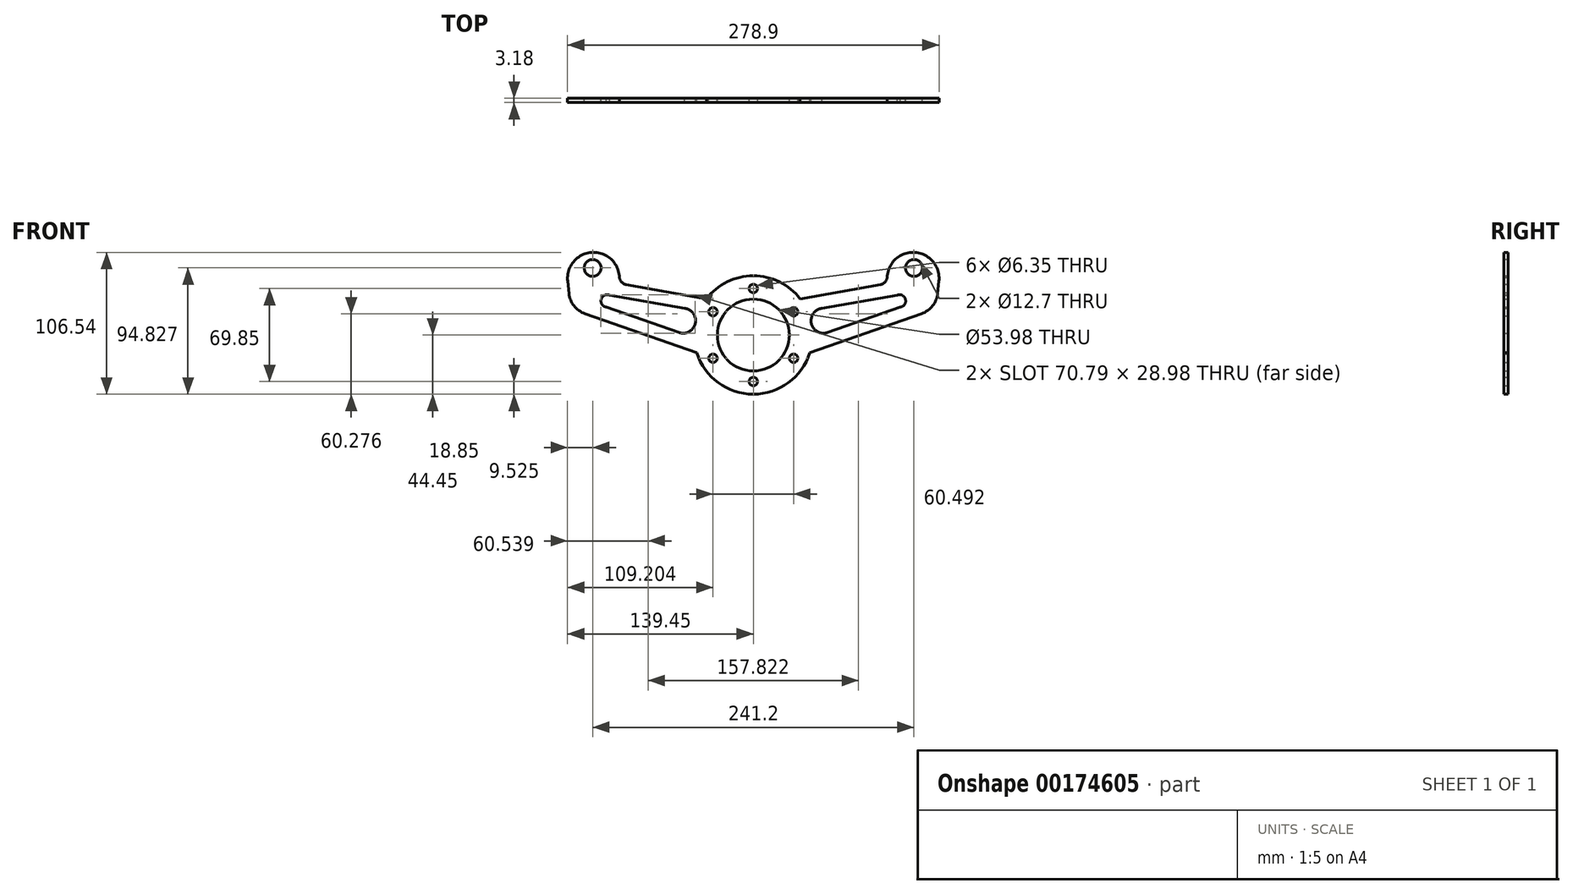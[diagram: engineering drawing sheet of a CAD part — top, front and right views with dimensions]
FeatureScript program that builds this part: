
annotation { "Feature Type Name" : "Feature", "Feature Type Description" : "" }
export const myFeature = defineFeature(function(context is Context, id is Id, definition is map)
    precondition{}
    {
        {
            var Q0;
            Q0=qCreatedBy(makeId("Front.planeOp"),FACE);
            var sketch = newSketch(context, id + "F0", { "sketchPlane" : qUnion([Q0])});
            skLineSegment(sketch, "E0", {"start": v(-35.2, 27.14) * mm, "end": v(-95.27, 37.77) * mm});
            skCircle(sketch, "E1", {"center": v(0, 34.93) * mm, "radius": 3.18 * mm});
            skCircle(sketch, "E2", {"center": v(-30.25, 17.46) * mm, "radius": 3.18 * mm});
            skCircle(sketch, "E3", {"center": v(-30.25, -17.46) * mm, "radius": 3.18 * mm});
            skCircle(sketch, "E4", {"center": v(0, -34.93) * mm, "radius": 3.18 * mm});
            skCircle(sketch, "E5", {"center": v(30.25, -17.46) * mm, "radius": 3.18 * mm});
            skCircle(sketch, "E6", {"center": v(30.25, 17.46) * mm, "radius": 3.18 * mm});
            skCircle(sketch, "E7", {"center": v(0, 0) * mm, "radius": 26.99 * mm});
            skCircle(sketch, "E8", {"center": v(-120.6, 50.38) * mm, "radius": 6.35 * mm});
            skArc(sketch, "E9.filletArc", {"start": v(-100.47, 43.26) * mm, "mid": v(-98.77, 39.66) * mm, "end": v(-95.27, 37.77) * mm});
            skArc(sketch, "E10.MirrorCS", {"start": v(100.47, 43.26) * mm, "mid": v(121.33, 62.04) * mm, "end": v(139.34, 40.51) * mm});
            skCircle(sketch, "E11.MirrorC", {"center": v(120.6, 50.38) * mm, "radius": 6.35 * mm});
            skArc(sketch, "E12.MirrorCS", {"start": v(100.47, 43.26) * mm, "mid": v(98.77, 39.66) * mm, "end": v(95.27, 37.77) * mm});
            skLineSegment(sketch, "E13.MirrorCS", {"start": v(35.2, 27.14) * mm, "end": v(95.27, 37.77) * mm});
            skArc(sketch, "E14.MirrorCS", {"start": v(138.35, 31.3) * mm, "mid": v(134.53, 21.89) * mm, "end": v(126.25, 15.99) * mm});
            skLineSegment(sketch, "E15", {"start": v(138.35, 31.3) * mm, "end": v(139.34, 40.51) * mm});
            skCircle(sketch, "E16", {"center": v(0, 0) * mm, "radius": 44.45 * mm});
            skLineSegment(sketch, "E17", {"start": v(-126.25, 15.99) * mm, "end": v(-42.42, -13.29) * mm});
            skLineSegment(sketch, "E18", {"start": v(126.25, 15.99) * mm, "end": v(42.42, -13.29) * mm});
            skLineSegment(sketch, "E19.MirrorCS", {"start": v(-138.35, 31.3) * mm, "end": v(-139.34, 40.51) * mm});
            skArc(sketch, "E20.MirrorCS", {"start": v(-138.35, 31.3) * mm, "mid": v(-134.53, 21.89) * mm, "end": v(-126.25, 15.99) * mm});
            skArc(sketch, "E21.MirrorCS", {"start": v(-100.47, 43.26) * mm, "mid": v(-121.33, 62.04) * mm, "end": v(-139.34, 40.51) * mm});
            skLineSegment(sketch, "E22", {"start": v(-55.85, 1.83) * mm, "end": v(-111.85, 21.38) * mm});
            skLineSegment(sketch, "E23", {"start": v(-50.63, 19.88) * mm, "end": v(-109.65, 30.32) * mm});
            skArc(sketch, "E24", {"start": v(-55.85, 1.83) * mm, "mid": v(-43.6, 8.57) * mm, "end": v(-51.6, 20.05) * mm});
            skPoint(sketch, "E24.first.point", {"position": v(-50.63, 19.88) * mm});
            skPoint(sketch, "E24.second.point", {"position": v(-43.69, 8.2) * mm});
            skPoint(sketch, "E24.third.point", {"position": v(-55.85, 1.83) * mm});
            skArc(sketch, "E25", {"start": v(-107.94, 30.02) * mm, "mid": v(-114.19, 26.84) * mm, "end": v(-110.46, 20.9) * mm});
            skPoint(sketch, "E25.first.point", {"position": v(-107.94, 30.02) * mm});
            skPoint(sketch, "E25.second.point", {"position": v(-111.85, 21.38) * mm});
            skLineSegment(sketch, "E26.MirrorCS", {"start": v(50.63, 19.88) * mm, "end": v(109.65, 30.32) * mm});
            skArc(sketch, "E27.MirrorCS", {"start": v(55.85, 1.83) * mm, "mid": v(43.6, 8.57) * mm, "end": v(51.6, 20.05) * mm});
            skLineSegment(sketch, "E28.MirrorCS", {"start": v(55.85, 1.83) * mm, "end": v(111.85, 21.38) * mm});
            skArc(sketch, "E29.MirrorCS", {"start": v(107.94, 30.02) * mm, "mid": v(114.19, 26.84) * mm, "end": v(110.46, 20.9) * mm});
            skSolve(sketch);
        }
        {
            var Q0;
            Q0 = qSketchRegion(id + "F0", true);
            var Q1;
            Q1=makeQuery(id+"F0.imprint","IMPRINT",FACE,{"disambiguationData":[TD([[makeQuery(id+"F0.imprint","IMPRINT",EDGE,{"derivedFrom":sQuery(id+"F0.wireOp",EDGE,"8sX9J035-qPig-24wR-7jH2-A3Y3Fydt0Jcw")}),1.0]])]});
            extrude(context, id + "F1", {"entities" : qUnion([Q0, Q1]), "depth" : 3.17 * mm});
        }
    });
